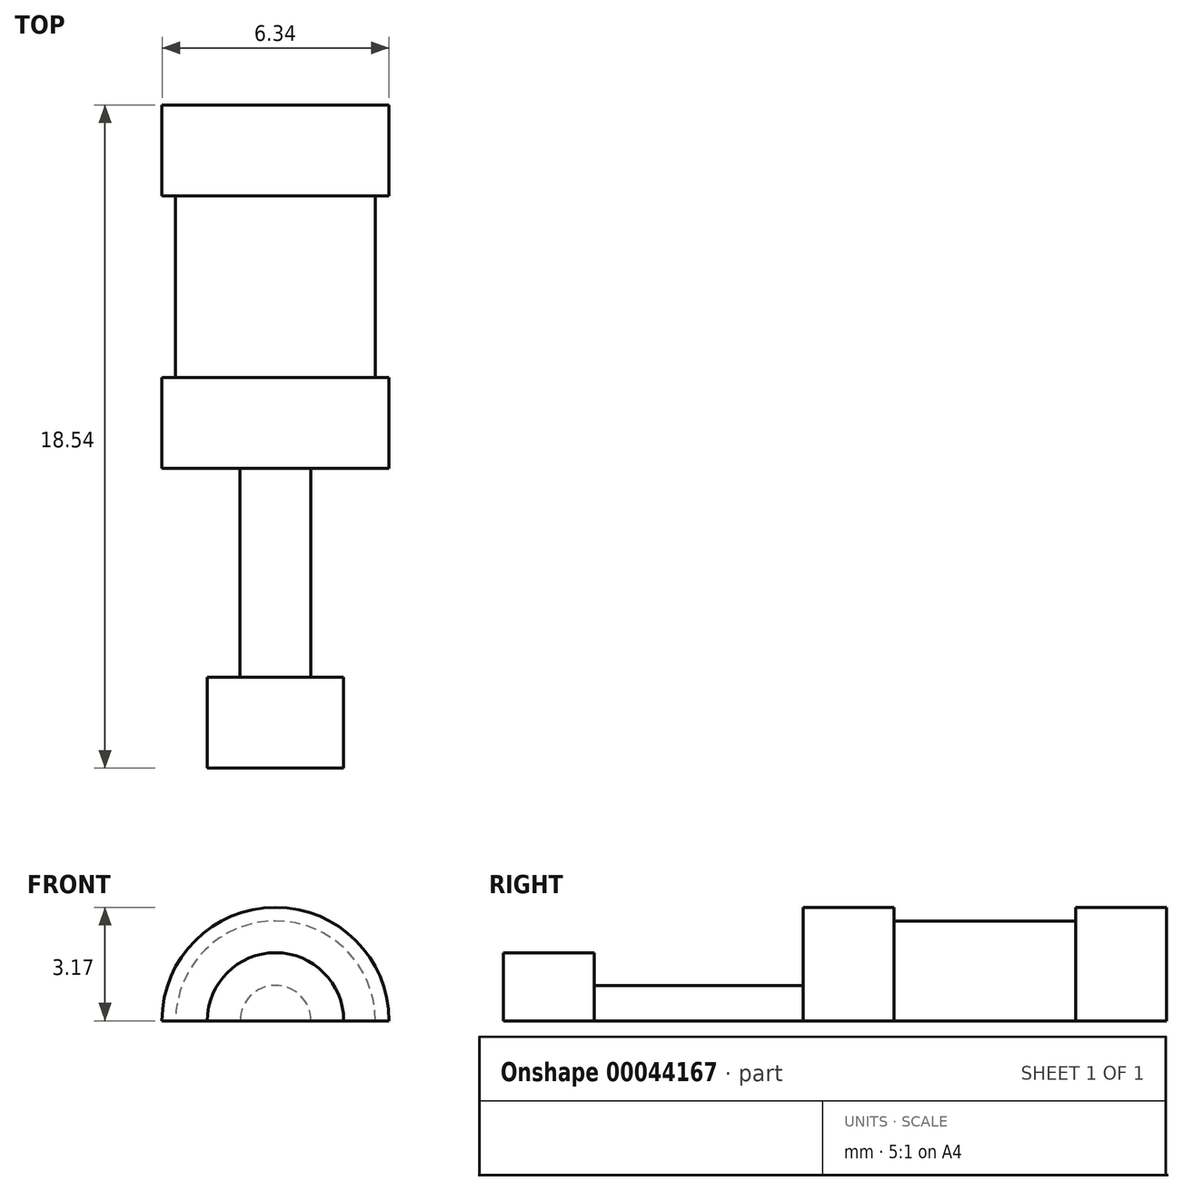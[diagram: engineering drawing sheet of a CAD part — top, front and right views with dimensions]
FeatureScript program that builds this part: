
annotation { "Feature Type Name" : "Feature", "Feature Type Description" : "" }
export const myFeature = defineFeature(function(context is Context, id is Id, definition is map)
    precondition{}
    {
        {
            var Q0;
            Q0=qCreatedBy(makeId("Right.planeOp"),FACE);
            var sketch = newSketch(context, id + "F0", { "sketchPlane" : qUnion([Q0])});
            skLineSegment(sketch, "E0", {"start": v(0, 0) * mm, "end": v(-18.54, 0) * mm});
            skLineSegment(sketch, "E1", {"start": v(-18.54, 0) * mm, "end": v(-18.54, 1.9) * mm});
            skLineSegment(sketch, "E2", {"start": v(-18.54, 1.9) * mm, "end": v(-16, 1.9) * mm});
            skLineSegment(sketch, "E3", {"start": v(-16, 1.9) * mm, "end": v(-16, 1) * mm});
            skLineSegment(sketch, "E4", {"start": v(-16, 1) * mm, "end": v(-10.16, 1) * mm});
            skLineSegment(sketch, "E5", {"start": v(-10.16, 1) * mm, "end": v(-10.16, 3.17) * mm});
            skLineSegment(sketch, "E6", {"start": v(-10.16, 3.17) * mm, "end": v(-7.62, 3.17) * mm});
            skLineSegment(sketch, "E7", {"start": v(-7.62, 3.17) * mm, "end": v(-7.62, 2.8) * mm});
            skLineSegment(sketch, "E8", {"start": v(0, 0) * mm, "end": v(0, 3.17) * mm});
            skLineSegment(sketch, "E9", {"start": v(0, 3.17) * mm, "end": v(-2.54, 3.17) * mm});
            skLineSegment(sketch, "E10", {"start": v(-2.54, 3.17) * mm, "end": v(-2.54, 2.8) * mm});
            skLineSegment(sketch, "E11", {"start": v(-2.54, 2.8) * mm, "end": v(-7.62, 2.8) * mm});
            skSolve(sketch);
        }
        {
            var Q0;
            Q0=makeQuery(id+"F0.imprint","IMPRINT",FACE,{"disambiguationData":[TD([[makeQuery(id+"F0.imprint","IMPRINT",EDGE,{"derivedFrom":sQuery(id+"F0.wireOp",EDGE,"E0")}),-1.0]])]});
            var Q1;
            Q1=sQuery(id+"F0.wireOp",EDGE,"E0");
            revolve(context, id + "F1", {"entities" : qUnion([Q0]), "axis" : qUnion([Q1]), "revolveType" : RevolveType.SYMMETRIC, "angle" : 180 * degree});
        }
    });
